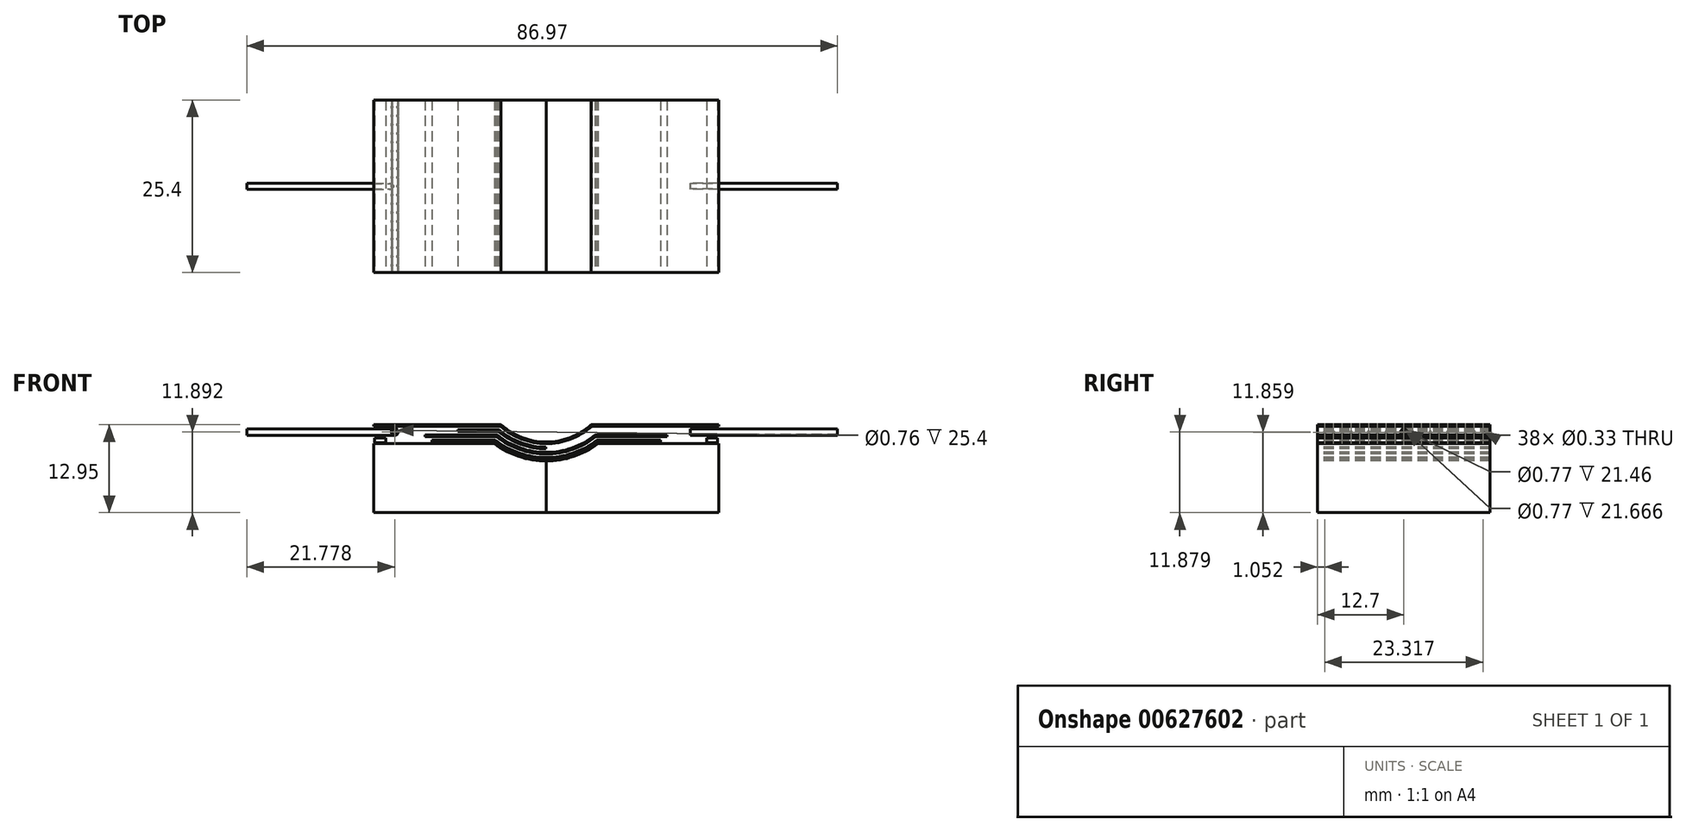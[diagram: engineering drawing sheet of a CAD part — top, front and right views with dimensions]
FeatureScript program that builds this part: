
annotation { "Feature Type Name" : "Feature", "Feature Type Description" : "" }
export const myFeature = defineFeature(function(context is Context, id is Id, definition is map)
    precondition{}
    {
        {
            var Q0;
            Q0=qCreatedBy(makeId("Front.planeOp"),FACE);
            var sketch = newSketch(context, id + "F0", { "sketchPlane" : qUnion([Q0])});
            skLineSegment(sketch, "E0", {"start": v(0, 0) * mm, "end": v(-25.4, 0) * mm});
            skLineSegment(sketch, "E1", {"start": v(-25.4, 0) * mm, "end": v(-25.4, 10.16) * mm});
            skLineSegment(sketch, "E2", {"start": v(-25.4, 10.16) * mm, "end": v(-7.62, 10.16) * mm});
            skArc(sketch, "E3", {"start": v(-7.62, 10.16) * mm, "mid": v(-4.02, 8.27) * mm, "end": v(0, 7.62) * mm});
            skLineSegment(sketch, "E4", {"start": v(0, 0) * mm, "end": v(0, 7.62) * mm});
            skArc(sketch, "E5.0", {"start": v(-6.72, 12.7) * mm, "mid": v(-3.6, 10.82) * mm, "end": v(0, 10.16) * mm});
            skLineSegment(sketch, "E5.1", {"start": v(-25.4, 12.7) * mm, "end": v(-6.72, 12.7) * mm});
            skArc(sketch, "E6.0", {"start": v(-6.62, 12.95) * mm, "mid": v(-3.55, 11.07) * mm, "end": v(0, 10.41) * mm});
            skLineSegment(sketch, "E6.1", {"start": v(-25.4, 12.95) * mm, "end": v(-6.62, 12.95) * mm});
            skLineSegment(sketch, "E7", {"start": v(0, 10.16) * mm, "end": v(0, 10.41) * mm});
            skLineSegment(sketch, "E8", {"start": v(-25.4, 12.95) * mm, "end": v(-25.4, 12.7) * mm});
            skLineSegment(sketch, "E9.bottom", {"start": v(-25.24, 10.33) * mm, "end": v(-23.62, 10.33) * mm});
            skLineSegment(sketch, "E9.top", {"start": v(-25.24, 10.98) * mm, "end": v(-23.62, 10.98) * mm});
            skLineSegment(sketch, "E9.left", {"start": v(-25.24, 10.33) * mm, "end": v(-25.24, 10.98) * mm});
            skLineSegment(sketch, "E9.right", {"start": v(-23.62, 10.33) * mm, "end": v(-23.62, 10.98) * mm});
            skArc(sketch, "E10.0", {"start": v(-7.53, 10.41) * mm, "mid": v(-3.98, 8.53) * mm, "end": v(0, 7.87) * mm});
            skLineSegment(sketch, "E10.1", {"start": v(-16.8, 10.41) * mm, "end": v(-7.53, 10.41) * mm});
            skArc(sketch, "E11.0", {"start": v(-7.45, 10.67) * mm, "mid": v(-3.93, 8.78) * mm, "end": v(0, 8.13) * mm});
            skLineSegment(sketch, "E12", {"start": v(-16.8, 10.67) * mm, "end": v(-16.8, 10.41) * mm});
            skLineSegment(sketch, "E13.trimOffspring", {"start": v(-16.8, 10.67) * mm, "end": v(-7.45, 10.67) * mm});
            skLineSegment(sketch, "E14", {"start": v(0, 8.13) * mm, "end": v(0, 7.87) * mm});
            skArc(sketch, "E15.0", {"start": v(-7.27, 11.18) * mm, "mid": v(-3.85, 9.29) * mm, "end": v(0, 8.64) * mm});
            skLineSegment(sketch, "E15.1", {"start": v(-17.82, 11.18) * mm, "end": v(-7.27, 11.18) * mm});
            skArc(sketch, "E16.0", {"start": v(-7.18, 11.43) * mm, "mid": v(-3.81, 9.54) * mm, "end": v(0, 8.89) * mm});
            skLineSegment(sketch, "E16.1", {"start": v(-17.82, 11.43) * mm, "end": v(-7.18, 11.43) * mm});
            skLineSegment(sketch, "E17", {"start": v(-17.82, 11.43) * mm, "end": v(-17.82, 11.18) * mm});
            skLineSegment(sketch, "E18", {"start": v(0, 8.9) * mm, "end": v(0, 8.64) * mm});
            skArc(sketch, "E19.0", {"start": v(-7, 11.94) * mm, "mid": v(-3.74, 10.06) * mm, "end": v(-0.02, 9.4) * mm});
            skArc(sketch, "E20.0", {"start": v(-6.93, 12.2) * mm, "mid": v(-3.7, 10.31) * mm, "end": v(-0.02, 9.65) * mm});
            skLineSegment(sketch, "E21", {"start": v(-0.02, 9.65) * mm, "end": v(-0.02, 9.4) * mm});
            skCircle(sketch, "E22", {"center": v(-22.3, 11.9) * mm, "radius": 0.38 * mm});
            skCircle(sketch, "E23.0", {"center": v(-22.3, 11.9) * mm, "radius": 0.5 * mm});
            skLineSegment(sketch, "E24", {"start": v(-12.97, 11.94) * mm, "end": v(-7, 11.94) * mm});
            skLineSegment(sketch, "E25", {"start": v(-12.97, 11.94) * mm, "end": v(-12.97, 12.2) * mm});
            skLineSegment(sketch, "E26", {"start": v(-12.97, 12.2) * mm, "end": v(-6.93, 12.2) * mm});
            skSolve(sketch);
        }
        {
            var Q0;
            Q0=makeQuery(id+"F0.imprint","IMPRINT",FACE,{"disambiguationData":[TD([[makeQuery(id+"F0.imprint","IMPRINT",EDGE,{"derivedFrom":sQuery(id+"F0.wireOp",EDGE,"E5.0")}),1.0]])]});
            var Q1;
            Q1=makeQuery(id+"F0.imprint","IMPRINT",FACE,{"disambiguationData":[TD([[makeQuery(id+"F0.imprint","IMPRINT",EDGE,{"derivedFrom":sQuery(id+"F0.wireOp",EDGE,"E9.bottom")}),1.0]])]});
            var Q2;
            Q2=makeQuery(id+"F0.imprint","IMPRINT",FACE,{"disambiguationData":[TD([[makeQuery(id+"F0.imprint","IMPRINT",EDGE,{"derivedFrom":sQuery(id+"F0.wireOp",EDGE,"E10.0")}),1.0]])]});
            var Q3;
            Q3=makeQuery(id+"F0.imprint","IMPRINT",FACE,{"disambiguationData":[TD([[makeQuery(id+"F0.imprint","IMPRINT",EDGE,{"derivedFrom":sQuery(id+"F0.wireOp",EDGE,"E0")}),-1.0]])]});
            var Q4;
            Q4=makeQuery(id+"F0.imprint","IMPRINT",FACE,{"disambiguationData":[TD([[makeQuery(id+"F0.imprint","IMPRINT",EDGE,{"derivedFrom":sQuery(id+"F0.wireOp",EDGE,"E15.0")}),1.0]])]});
            var Q5;
            Q5=makeQuery(id+"F0.imprint","IMPRINT",FACE,{"disambiguationData":[TD([[makeQuery(id+"F0.imprint","IMPRINT",EDGE,{"derivedFrom":sQuery(id+"F0.wireOp",EDGE,"E19.0")}),1.0]])]});
            var Q6;
            Q6=makeQuery(id+"F0.imprint","IMPRINT",FACE,{"disambiguationData":[TD([[makeQuery(id+"F0.imprint","IMPRINT",EDGE,{"derivedFrom":sQuery(id+"F0.wireOp",EDGE,"E22")}),-1.0]])]});
            extrude(context, id + "F1", {"entities" : qUnion([Q0, Q1, Q2, Q3, Q4, Q5, Q6]), "oppositeDirection" : true, "depth" : 25.4 * mm, "offsetDistance" : 25.4 * mm});
        }
        {
            var Q0;
            Q0=makeQuery(id+"F1.opExtrude","SWEPT_BODY",BODY,{"disambiguationData":[OSD([sQuery(id+"F0.wireOp",EDGE,"E0"),sQuery(id+"F0.wireOp",EDGE,"E1"),sQuery(id+"F0.wireOp",EDGE,"E2"),sQuery(id+"F0.wireOp",EDGE,"E3"),sQuery(id+"F0.wireOp",EDGE,"E4")])]});
            var Q1;
            Q1=makeQuery(id+"F1.opExtrude","SWEPT_BODY",BODY,{"disambiguationData":[OSD([sQuery(id+"F0.wireOp",EDGE,"E5.0"),sQuery(id+"F0.wireOp",EDGE,"E5.1"),sQuery(id+"F0.wireOp",EDGE,"E6.0"),sQuery(id+"F0.wireOp",EDGE,"E6.1"),sQuery(id+"F0.wireOp",EDGE,"E7"),sQuery(id+"F0.wireOp",EDGE,"E8")])]});
            var Q2;
            Q2=makeQuery(id+"F1.opExtrude","SWEPT_BODY",BODY,{"disambiguationData":[OSD([sQuery(id+"F0.wireOp",EDGE,"E9.bottom"),sQuery(id+"F0.wireOp",EDGE,"E9.top"),sQuery(id+"F0.wireOp",EDGE,"E9.left"),sQuery(id+"F0.wireOp",EDGE,"E9.right")])]});
            var Q3;
            Q3=makeQuery(id+"F1.opExtrude","SWEPT_BODY",BODY,{"disambiguationData":[OSD([sQuery(id+"F0.wireOp",EDGE,"E10.0"),sQuery(id+"F0.wireOp",EDGE,"E10.1"),sQuery(id+"F0.wireOp",EDGE,"E11.0"),sQuery(id+"F0.wireOp",EDGE,"E12"),sQuery(id+"F0.wireOp",EDGE,"E13.trimOffspring"),sQuery(id+"F0.wireOp",EDGE,"E14")])]});
            var Q4;
            Q4=makeQuery(id+"F1.opExtrude","SWEPT_BODY",BODY,{"disambiguationData":[OSD([sQuery(id+"F0.wireOp",EDGE,"E15.0"),sQuery(id+"F0.wireOp",EDGE,"E15.1"),sQuery(id+"F0.wireOp",EDGE,"E16.0"),sQuery(id+"F0.wireOp",EDGE,"E16.1"),sQuery(id+"F0.wireOp",EDGE,"E17"),sQuery(id+"F0.wireOp",EDGE,"E18")])]});
            var Q5;
            Q5=makeQuery(id+"F1.opExtrude","SWEPT_FACE",FACE,{"disambiguationData":[OSD([sQuery(id+"F0.wireOp",EDGE,"E4")])]});
            mirror(context, id + "F2", {"operationType" : NewBodyOperationType.ADD, "entities" : qUnion([Q0, Q1, Q2, Q3, Q4]), "mirrorPlane" : qUnion([Q5])});
        }
        {
            var Q0;
            Q0=makeQuery(id+"F1.opExtrude","SWEPT_FACE",FACE,{"disambiguationData":[OSD([sQuery(id+"F0.wireOp",EDGE,"E1")])]});
            var sketch = newSketch(context, id + "F3", { "sketchPlane" : qUnion([Q0])});
            skCircle(sketch, "E27", {"center": v(-12.7, 11.88) * mm, "radius": 0.47 * mm});
            skCircle(sketch, "E28", {"center": v(-12.7, 11.88) * mm, "radius": 0.38 * mm});
            skLineSegment(sketch, "E29", {"start": v(-25.4, 0) * mm, "end": v(0, 0) * mm, "construction": true});
            skLineSegment(sketch, "E30", {"start": v(-12.7, 0) * mm, "end": v(-12.7, 13.86) * mm, "construction": true});
            skSolve(sketch);
        }
        {
            var Q0;
            Q0=makeQuery(id+"F3.imprint","IMPRINT",FACE,{"disambiguationData":[TD([[makeQuery(id+"F3.imprint","IMPRINT",EDGE,{"derivedFrom":sQuery(id+"F3.wireOp",EDGE,"E27")}),1.0]])]});
            extrude(context, id + "F4", {"entities" : qUnion([Q0]), "operationType" : NewBodyOperationType.ADD, "depth" : 18.67 * mm, "offsetDistance" : 25.4 * mm, "hasSecondDirection" : true, "secondDirectionBound" : SecondDirectionBoundingType.UP_TO_NEXT, "secondDirectionOppositeDirection" : true, "secondDirectionDepth" : 25.4 * mm});
        }
        {
            var Q0;
            Q0=makeQuery(id+"F1.opExtrude","SWEPT_FACE",FACE,{"disambiguationData":[OSD([sQuery(id+"F0.wireOp",EDGE,"E1")])]});
            var sketch = newSketch(context, id + "F5", { "sketchPlane" : qUnion([Q0])});
            skLineSegment(sketch, "E31", {"start": v(-25.45, 11.86) * mm, "end": v(0, 11.86) * mm, "construction": true});
            skCircle(sketch, "E32", {"center": v(-24.37, 11.86) * mm, "radius": 0.17 * mm});
            skCircle(sketch, "E33.1.0.0", {"center": v(-23.07, 11.86) * mm, "radius": 0.17 * mm});
            skCircle(sketch, "E33.2.0.0", {"center": v(-21.78, 11.86) * mm, "radius": 0.17 * mm});
            skCircle(sketch, "E33.3.0.0", {"center": v(-20.48, 11.86) * mm, "radius": 0.17 * mm});
            skCircle(sketch, "E33.4.0.0", {"center": v(-19.19, 11.86) * mm, "radius": 0.17 * mm});
            skCircle(sketch, "E33.5.0.0", {"center": v(-17.9, 11.86) * mm, "radius": 0.17 * mm});
            skCircle(sketch, "E33.6.0.0", {"center": v(-16.6, 11.86) * mm, "radius": 0.17 * mm});
            skCircle(sketch, "E33.7.0.0", {"center": v(-15.3, 11.86) * mm, "radius": 0.17 * mm});
            skCircle(sketch, "E33.8.0.0", {"center": v(-14, 11.86) * mm, "radius": 0.17 * mm});
            skCircle(sketch, "E33.9.0.0", {"center": v(-12.71, 11.86) * mm, "radius": 0.17 * mm});
            skCircle(sketch, "E33.10.0.0", {"center": v(-11.41, 11.86) * mm, "radius": 0.17 * mm});
            skCircle(sketch, "E33.11.0.0", {"center": v(-10.12, 11.86) * mm, "radius": 0.17 * mm});
            skCircle(sketch, "E33.12.0.0", {"center": v(-8.82, 11.86) * mm, "radius": 0.17 * mm});
            skCircle(sketch, "E33.13.0.0", {"center": v(-7.53, 11.86) * mm, "radius": 0.17 * mm});
            skCircle(sketch, "E33.14.0.0", {"center": v(-6.23, 11.86) * mm, "radius": 0.17 * mm});
            skCircle(sketch, "E33.15.0.0", {"center": v(-4.94, 11.86) * mm, "radius": 0.17 * mm});
            skCircle(sketch, "E33.16.0.0", {"center": v(-3.64, 11.86) * mm, "radius": 0.17 * mm});
            skCircle(sketch, "E33.17.0.0", {"center": v(-2.35, 11.86) * mm, "radius": 0.17 * mm});
            skCircle(sketch, "E33.18.0.0", {"center": v(-1.05, 11.86) * mm, "radius": 0.17 * mm});
            skLineSegment(sketch, "E33.direction1", {"start": v(-24.37, 11.86) * mm, "end": v(-23.07, 11.86) * mm, "construction": true});
            skSolve(sketch);
        }
        {
            var Q0;
            Q0 = qSketchRegion(id + "F5", true);
            extrude(context, id + "F6", {"entities" : qUnion([Q0]), "operationType" : NewBodyOperationType.REMOVE, "oppositeDirection" : true, "depth" : 5.66 * mm, "offsetDistance" : 25.4 * mm});
        }
        {
            var Q0;
            Q0 = qSketchRegion(id + "F3", true);
            extrude(context, id + "F7", {"entities" : qUnion([Q0]), "oppositeDirection" : true, "depth" : 68.3 * mm, "offsetDistance" : 25.4 * mm, "hasSecondDirection" : true, "secondDirectionOppositeDirection" : true, "secondDirectionDepth" : 46.63 * mm});
        }
    });
